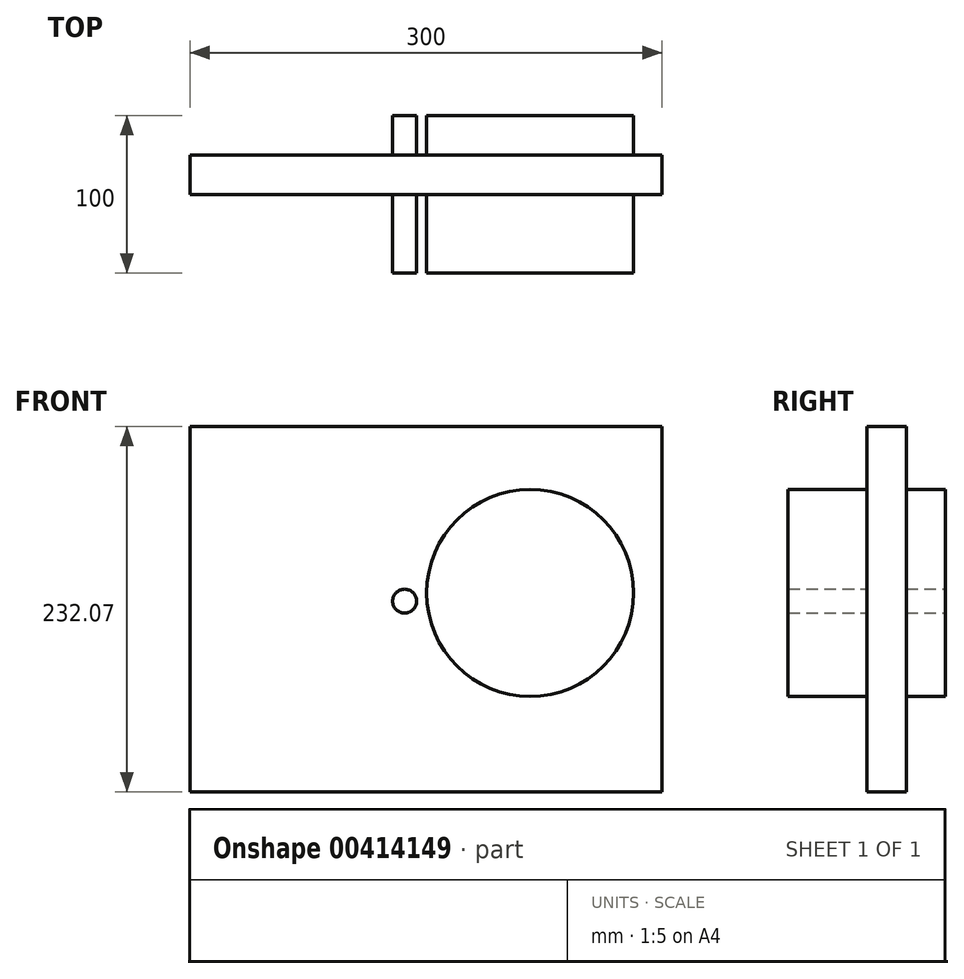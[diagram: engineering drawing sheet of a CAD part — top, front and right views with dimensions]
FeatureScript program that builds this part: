
annotation { "Feature Type Name" : "Feature", "Feature Type Description" : "" }
export const myFeature = defineFeature(function(context is Context, id is Id, definition is map)
    precondition{}
    {
        {
            var Q0;
            Q0=qCreatedBy(makeId("Front.planeOp"),FACE);
            var sketch = newSketch(context, id + "F0", { "sketchPlane" : qUnion([Q0])});
            skLineSegment(sketch, "E0.bottom", {"start": v(-159.55, 104.23) * mm, "end": v(140.45, 104.23) * mm});
            skLineSegment(sketch, "E0.top", {"start": v(-159.55, -127.84) * mm, "end": v(140.45, -127.84) * mm});
            skLineSegment(sketch, "E0.left", {"start": v(-159.55, 104.23) * mm, "end": v(-159.55, -127.84) * mm});
            skLineSegment(sketch, "E0.right", {"start": v(140.45, 104.23) * mm, "end": v(140.45, -127.84) * mm});
            skSolve(sketch);
        }
        {
            var Q0;
            Q0 = qSketchRegion(id + "F0", true);
            extrude(context, id + "F1", {"entities" : qUnion([Q0]), "depth" : 25 * mm});
        }
        {
            var Q0;
            Q0=makeQuery(id+"F1.opExtrude","CAP_FACE",FACE,{"disambiguationData":[OSD([sQuery(id+"F0.wireOp",EDGE,"E0.bottom"),sQuery(id+"F0.wireOp",EDGE,"E0.top"),sQuery(id+"F0.wireOp",EDGE,"E0.left"),sQuery(id+"F0.wireOp",EDGE,"E0.right")])],"isStart":false});
            var sketch = newSketch(context, id + "F2", { "sketchPlane" : qUnion([Q0])});
            skCircle(sketch, "E1", {"center": v(-23.16, -6.7) * mm, "radius": 7.6 * mm});
            skSolve(sketch);
        }
        {
            var Q0;
            Q0 = qSketchRegion(id + "F2", true);
            extrude(context, id + "F3", {"entities" : qUnion([Q0]), "operationType" : NewBodyOperationType.ADD, "endBound" : BoundingType.SYMMETRIC, "depth" : 100 * mm});
        }
        {
            var Q0;
            Q0=makeQuery(id+"F1.opExtrude","CAP_FACE",FACE,{"disambiguationData":[OSD([sQuery(id+"F0.wireOp",EDGE,"E0.bottom"),sQuery(id+"F0.wireOp",EDGE,"E0.top"),sQuery(id+"F0.wireOp",EDGE,"E0.left"),sQuery(id+"F0.wireOp",EDGE,"E0.right")])],"isStart":false});
            var sketch = newSketch(context, id + "F4", { "sketchPlane" : qUnion([Q0])});
            skCircle(sketch, "E2", {"center": v(56.6, -1.48) * mm, "radius": 65.71 * mm});
            skSolve(sketch);
        }
        {
            var Q0;
            Q0=makeQuery(id+"F4.imprint","IMPRINT",FACE,{"disambiguationData":[TD([[makeQuery(id+"F4.imprint","IMPRINT",EDGE,{"derivedFrom":sQuery(id+"F4.wireOp",EDGE,"E2")}),1.0]])]});
            var Q1;
            Q1=sQuery(id+"F4.wireOp",EDGE,"E2");
            extrude(context, id + "F5", {"entities" : qUnion([Q0]), "operationType" : NewBodyOperationType.ADD, "surfaceEntities" : qUnion([Q1]), "endBound" : BoundingType.SYMMETRIC, "depth" : 100 * mm});
        }
    });
